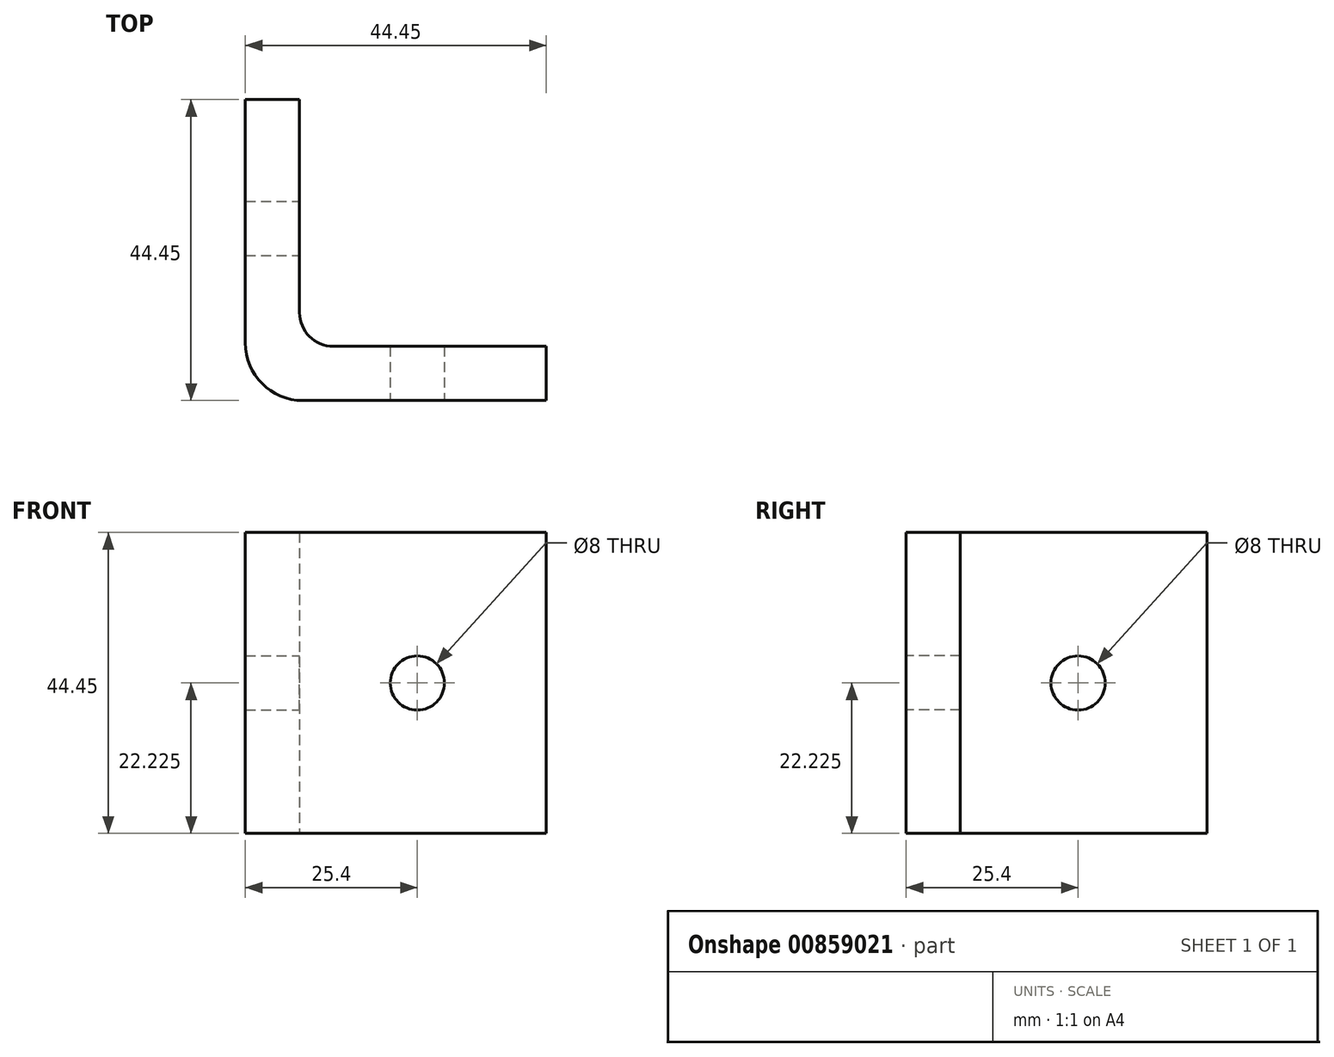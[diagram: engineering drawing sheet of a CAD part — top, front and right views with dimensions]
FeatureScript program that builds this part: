
annotation { "Feature Type Name" : "Feature", "Feature Type Description" : "" }
export const myFeature = defineFeature(function(context is Context, id is Id, definition is map)
    precondition{}
    {
        {
            var Q0;
            Q0=qCreatedBy(makeId("Top.planeOp"),FACE);
            var sketch = newSketch(context, id + "F0", { "sketchPlane" : qUnion([Q0])});
            skLineSegment(sketch, "E0", {"start": v(0, 44.45) * mm, "end": v(0, 8.5) * mm});
            skLineSegment(sketch, "E1", {"start": v(8.5, 0) * mm, "end": v(44.45, 0) * mm});
            skLineSegment(sketch, "E2", {"start": v(44.45, 0) * mm, "end": v(44.45, 8) * mm});
            skLineSegment(sketch, "E3", {"start": v(44.45, 8) * mm, "end": v(13, 8) * mm});
            skLineSegment(sketch, "E4", {"start": v(8, 13) * mm, "end": v(8, 44.45) * mm});
            skLineSegment(sketch, "E5", {"start": v(8, 44.45) * mm, "end": v(0, 44.45) * mm});
            skPoint(sketch, "E6.visualSharp", {"position": v(0, 0) * mm});
            skArc(sketch, "E6.filletArc", {"start": v(0, 8.5) * mm, "mid": v(2.49, 2.49) * mm, "end": v(8.5, 0) * mm});
            skPoint(sketch, "E7.visualSharp", {"position": v(8, 8) * mm});
            skArc(sketch, "E7.filletArc", {"start": v(8, 13) * mm, "mid": v(9.46, 9.46) * mm, "end": v(13, 8) * mm});
            skSolve(sketch);
        }
        {
            var Q0;
            Q0=qSketchRegion(id+"F0",true);
            extrude(context, id + "F1", {"entities" : qUnion([Q0]), "depth" : 44.45 * mm, "offsetDistance" : 25 * mm});
        }
        {
            var Q0;
            Q0=makeQuery(id+"F1.opExtrude","SWEPT_FACE",FACE,{"disambiguationData":[OSD([sQuery(id+"F0.wireOp",EDGE,"E4")])]});
            var sketch = newSketch(context, id + "F2", { "sketchPlane" : qUnion([Q0])});
            skLineSegment(sketch, "E8", {"start": v(44.45, 22.23) * mm, "end": v(0, 22.23) * mm, "construction": true});
            skCircle(sketch, "E9", {"center": v(25.4, 22.22) * mm, "radius": 4 * mm});
            skSolve(sketch);
        }
        {
            var Q0;
            Q0=qSketchRegion(id+"F2",true);
            extrude(context, id + "F3", {"entities" : qUnion([Q0]), "operationType" : NewBodyOperationType.REMOVE, "endBound" : BoundingType.UP_TO_NEXT, "oppositeDirection" : true, "depth" : 25 * mm, "offsetDistance" : 25 * mm});
        }
        {
            var Q0;
            Q0=makeQuery(id+"F1.opExtrude","SWEPT_FACE",FACE,{"disambiguationData":[OSD([sQuery(id+"F0.wireOp",EDGE,"E1")])]});
            var sketch = newSketch(context, id + "F4", { "sketchPlane" : qUnion([Q0])});
            skLineSegment(sketch, "E10", {"start": v(44.45, 22.23) * mm, "end": v(0, 22.23) * mm, "construction": true});
            skCircle(sketch, "E11", {"center": v(25.4, 22.22) * mm, "radius": 4 * mm});
            skSolve(sketch);
        }
        {
            var Q0;
            Q0=qSketchRegion(id+"F4",true);
            extrude(context, id + "F5", {"entities" : qUnion([Q0]), "operationType" : NewBodyOperationType.REMOVE, "endBound" : BoundingType.UP_TO_NEXT, "oppositeDirection" : true, "depth" : 25 * mm, "offsetDistance" : 25 * mm});
        }
    });
